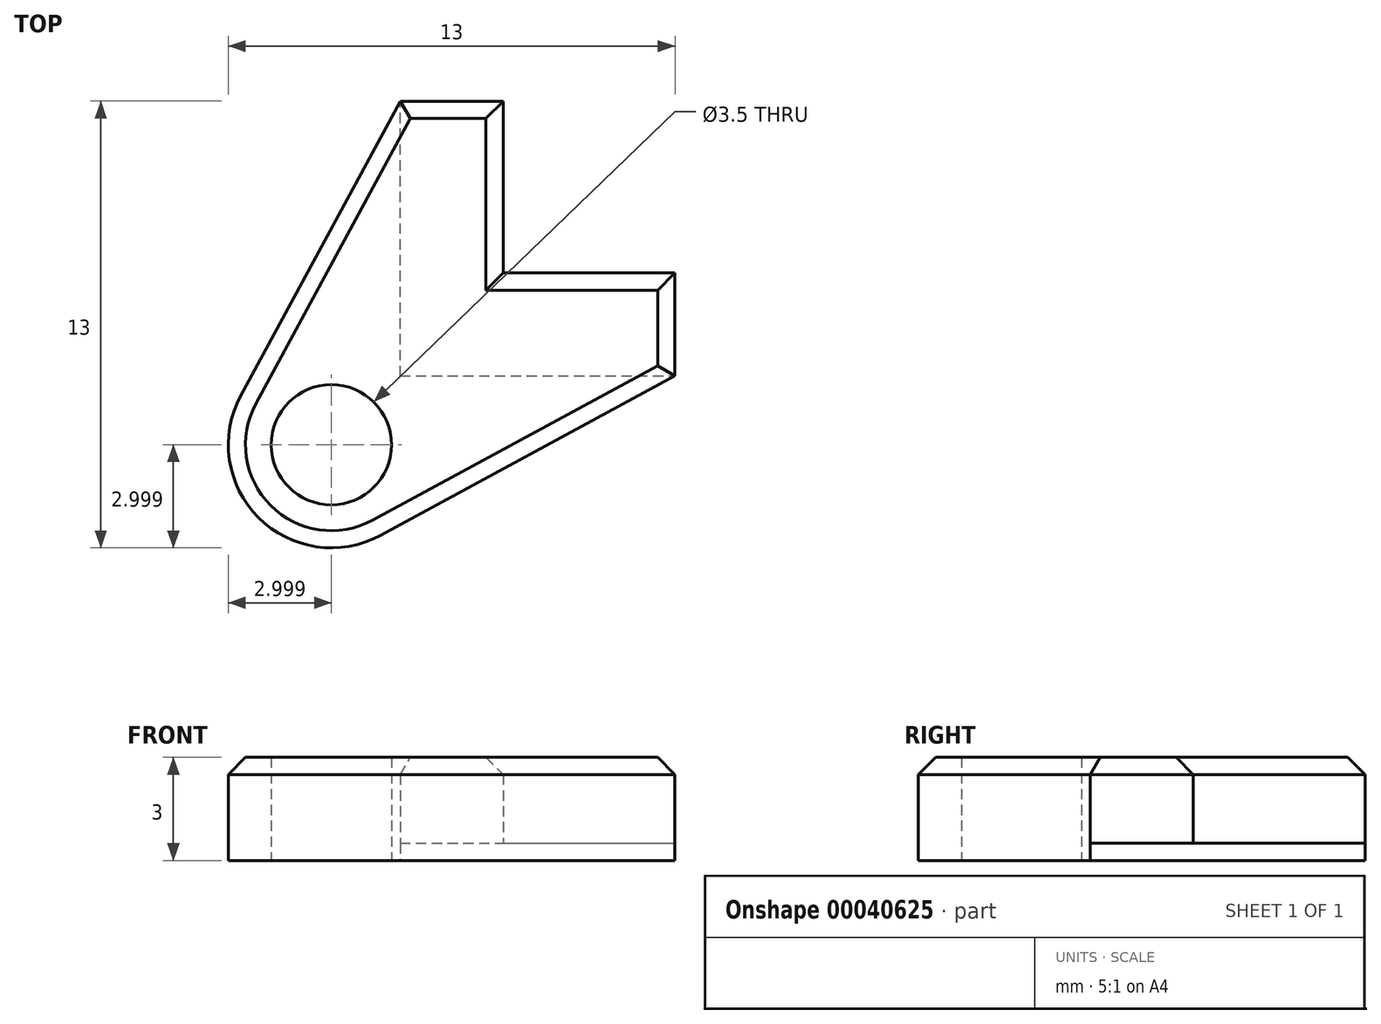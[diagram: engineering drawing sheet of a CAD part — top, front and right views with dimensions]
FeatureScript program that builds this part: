
annotation { "Feature Type Name" : "Feature", "Feature Type Description" : "" }
export const myFeature = defineFeature(function(context is Context, id is Id, definition is map)
    precondition{}
    {
        {
            var Q0;
            Q0=qCreatedBy(makeId("Top.planeOp"),FACE);
            var sketch = newSketch(context, id + "F0", { "sketchPlane" : qUnion([Q0])});
            skLineSegment(sketch, "E0.0", {"start": v(1.22, 1.22) * mm, "end": v(1.22, 6.22) * mm});
            skLineSegment(sketch, "E1.0", {"start": v(-1.78, 6.22) * mm, "end": v(1.22, 6.22) * mm});
            skLineSegment(sketch, "E2.0", {"start": v(6.22, -1.78) * mm, "end": v(6.22, 1.22) * mm});
            skLineSegment(sketch, "E3.0", {"start": v(-1.78, -1.78) * mm, "end": v(-1.78, 6.22) * mm});
            skLineSegment(sketch, "E4.0", {"start": v(-1.78, -1.78) * mm, "end": v(6.22, -1.78) * mm});
            skCircle(sketch, "E5", {"center": v(-3.78, -3.78) * mm, "radius": 1.75 * mm});
            skArc(sketch, "E6.0", {"start": v(-6.42, -2.35) * mm, "mid": v(-5.9, -5.9) * mm, "end": v(-2.35, -6.42) * mm});
            skLineSegment(sketch, "E7", {"start": v(-1.78, 6.22) * mm, "end": v(-6.42, -2.35) * mm});
            skLineSegment(sketch, "E8", {"start": v(6.22, -1.78) * mm, "end": v(-2.35, -6.42) * mm});
            skLineSegment(sketch, "E9.0", {"start": v(1.22, 1.22) * mm, "end": v(6.22, 1.22) * mm});
            skSolve(sketch);
        }
        {
            var Q0;
            Q0 = qSketchRegion(id + "F0", true);
            extrude(context, id + "F1", {"entities" : qUnion([Q0]), "depth" : 3 * mm});
        }
        {
            var Q0;
            Q0=makeQuery(id+"F0.imprint","IMPRINT",FACE,{"disambiguationData":[TD([[makeQuery(id+"F0.imprint","IMPRINT",EDGE,{"derivedFrom":sQuery(id+"F0.wireOp",EDGE,"E0.0")}),1.0]])]});
            extrude(context, id + "F2", {"entities" : qUnion([Q0]), "operationType" : NewBodyOperationType.REMOVE, "depth" : 0.5 * mm});
        }
        {
            var Q0;
            Q0=makeQuery(id+"F1.opExtrude","CAP_EDGE",EDGE,{"disambiguationData":[OSD([sQuery(id+"F0.wireOp",EDGE,"E8")])],"isStart":false});
            var Q1;
            Q1=makeQuery(id+"F1.opExtrude","CAP_EDGE",EDGE,{"disambiguationData":[OSD([sQuery(id+"F0.wireOp",EDGE,"E6.0")])],"isStart":false});
            var Q2;
            Q2=makeQuery(id+"F1.opExtrude","CAP_EDGE",EDGE,{"disambiguationData":[OSD([sQuery(id+"F0.wireOp",EDGE,"E7")])],"isStart":false});
            chamfer(context, id + "F3", {"entities" : qUnion([Q0, Q1, Q2]), "width" : .5 * mm, "tangentPropagation" : true});
        }
        {
            var Q0;
            Q0=makeQuery(id+"F1.opExtrude","CAP_EDGE",EDGE,{"disambiguationData":[OSD([sQuery(id+"F0.wireOp",EDGE,"E2.0")])],"isStart":false});
            var Q1;
            Q1=makeQuery(id+"F1.opExtrude","CAP_EDGE",EDGE,{"disambiguationData":[OSD([sQuery(id+"F0.wireOp",EDGE,"E9.0")])],"isStart":false});
            var Q2;
            Q2=makeQuery(id+"F1.opExtrude","CAP_EDGE",EDGE,{"disambiguationData":[OSD([sQuery(id+"F0.wireOp",EDGE,"E0.0")])],"isStart":false});
            var Q3;
            Q3=makeQuery(id+"F1.opExtrude","CAP_EDGE",EDGE,{"disambiguationData":[OSD([sQuery(id+"F0.wireOp",EDGE,"E1.0")])],"isStart":false});
            chamfer(context, id + "F4", {"entities" : qUnion([Q0, Q1, Q2, Q3]), "width" : .5 * mm, "tangentPropagation" : true});
        }
    });
